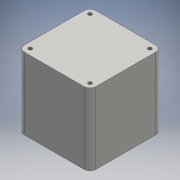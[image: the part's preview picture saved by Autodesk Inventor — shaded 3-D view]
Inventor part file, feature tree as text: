
AUTODESK INVENTOR PART (.ipt)
format: ipt  version: 2016 (Build 200138000, 138)  size: 107,520 bytes
history: native  units: mm
features: extrude x1, fillet x1, sketch x1
ambient origin geometry x8: Origin, YZ Plane, XZ Plane, XY Plane, X Axis, Y Axis, Z Axis, Center Point
bodies: Solid1 (feature_tree)
feature tree (3):
  extrude  "Block"  Depth=60.0mm
  fillet  "Fillets FTW"  Radius=5.0mm
  sketch  "Sketch1"  dims[d0=60.0mm d1=60.0mm d2=5.0mm d3=5.0mm d4=5.0mm d5=5.0mm d6=5.0mm d7=5.0mm d8=5.0mm d9=5.0mm d10=3.0mm d11=3.0mm d12=3.0mm d13=3.0mm d14=60.0mm d15=0.0mm d16=5.0mm]
